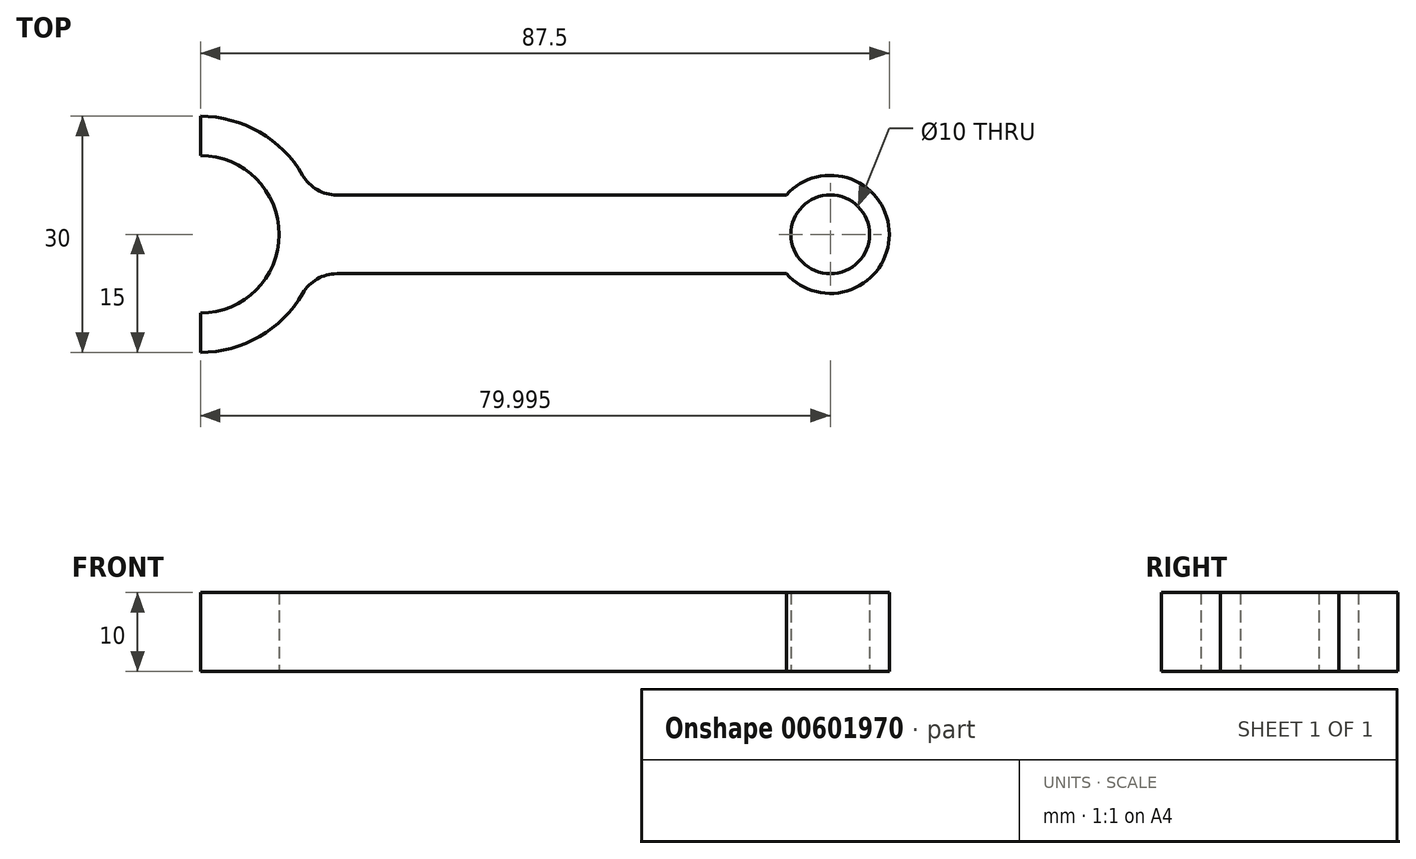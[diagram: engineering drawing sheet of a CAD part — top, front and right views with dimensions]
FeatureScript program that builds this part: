
annotation { "Feature Type Name" : "Feature", "Feature Type Description" : "" }
export const myFeature = defineFeature(function(context is Context, id is Id, definition is map)
    precondition{}
    {
        {
            var Q0;
            Q0=qCreatedBy(makeId("Top.planeOp"),FACE);
            var sketch = newSketch(context, id + "F0", { "sketchPlane" : qUnion([Q0])});
            skArc(sketch, "E0", {"start": v(-31.46, -10) * mm, "mid": v(-21.46, 0) * mm, "end": v(-31.46, 10) * mm});
            skCircle(sketch, "E1", {"center": v(48.54, 0) * mm, "radius": 5 * mm});
            skArc(sketch, "E2", {"start": v(-18.47, 7.5) * mm, "mid": v(-23.96, 13) * mm, "end": v(-31.46, 15) * mm});
            skArc(sketch, "E3", {"start": v(42.94, -5) * mm, "mid": v(56.04, 0) * mm, "end": v(42.94, 5) * mm});
            skLineSegment(sketch, "E4.bottom", {"start": v(-14.14, 5) * mm, "end": v(42.94, 5) * mm});
            skLineSegment(sketch, "E4.top", {"start": v(-14.14, -5) * mm, "end": v(42.94, -5) * mm});
            skLineSegment(sketch, "E5", {"start": v(-31.46, 15) * mm, "end": v(-31.46, 10) * mm});
            skArc(sketch, "E6.trimOffspring", {"start": v(-31.46, -15) * mm, "mid": v(-23.96, -13) * mm, "end": v(-18.47, -7.5) * mm});
            skLineSegment(sketch, "E7.trimOffspring", {"start": v(-31.46, -10) * mm, "end": v(-31.46, -15) * mm});
            skPoint(sketch, "E8.visualSharp", {"position": v(-17.32, -5) * mm});
            skArc(sketch, "E8.filletArc", {"start": v(-14.14, -5) * mm, "mid": v(-16.64, -5.67) * mm, "end": v(-18.47, -7.5) * mm});
            skPoint(sketch, "E9.visualSharp", {"position": v(-17.32, 5) * mm});
            skArc(sketch, "E9.filletArc", {"start": v(-18.47, 7.5) * mm, "mid": v(-16.64, 5.67) * mm, "end": v(-14.14, 5) * mm});
            skSolve(sketch);
        }
        {
            var Q0;
            Q0 = qSketchRegion(id + "F0", true);
            extrude(context, id + "F1", {"entities" : qUnion([Q0]), "depth" : 10 * mm, "offsetDistance" : 25 * mm});
        }
    });
